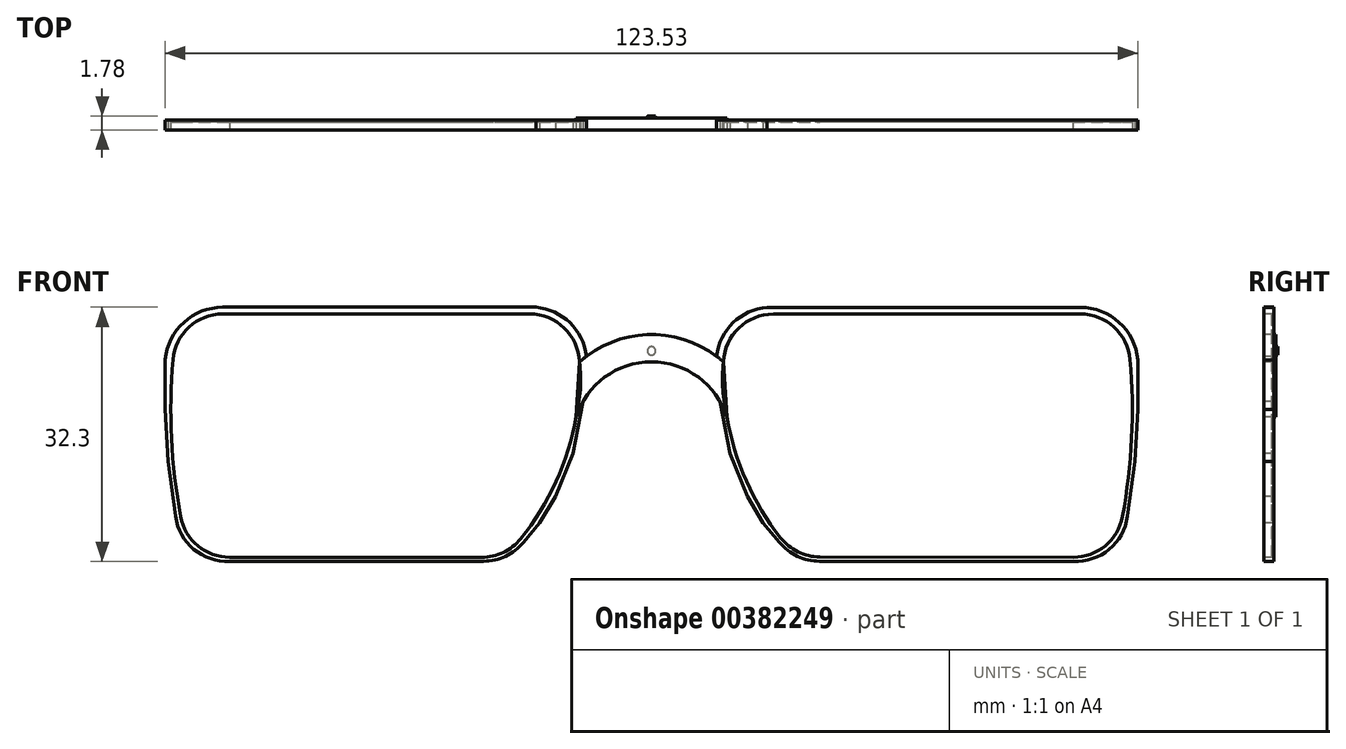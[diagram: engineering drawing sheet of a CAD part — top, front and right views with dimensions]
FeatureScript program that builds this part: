
annotation { "Feature Type Name" : "Feature", "Feature Type Description" : "" }
export const myFeature = defineFeature(function(context is Context, id is Id, definition is map)
    precondition{}
    {
        {
            var Q0;
            Q0=qCreatedBy(makeId("Front.planeOp"),FACE);
            var sketch = newSketch(context, id + "F0", { "sketchPlane" : qUnion([Q0])});
            skArc(sketch, "E0", {"start": v(-45.39, 36.1) * mm, "mid": v(-45.58, 26.1) * mm, "end": v(-44.42, 16.18) * mm});
            skLineSegment(sketch, "E1", {"start": v(-38.17, 11) * mm, "end": v(-6.15, 11) * mm});
            skLineSegment(sketch, "E2", {"start": v(-39.06, 41.9) * mm, "end": v(-0.1, 41.9) * mm});
            skPoint(sketch, "E3.visualSharp", {"position": v(-44.65, 41.9) * mm});
            skArc(sketch, "E3.filletArc", {"start": v(-39.06, 41.9) * mm, "mid": v(-43.35, 40.22) * mm, "end": v(-45.39, 36.1) * mm});
            skPoint(sketch, "E4.visualSharp", {"position": v(-43.25, 11) * mm});
            skArc(sketch, "E4.filletArc", {"start": v(-44.42, 16.18) * mm, "mid": v(-42.23, 12.46) * mm, "end": v(-38.17, 11) * mm});
            skArc(sketch, "E5", {"start": v(-1.23, 13.33) * mm, "mid": v(4.57, 23.88) * mm, "end": v(6.25, 35.8) * mm});
            skArc(sketch, "E6", {"start": v(24.99, 28.8) * mm, "mid": v(15.4, 35.8) * mm, "end": v(5.8, 28.8) * mm});
            skArc(sketch, "E7", {"start": v(24.54, 35.8) * mm, "mid": v(15.4, 39.27) * mm, "end": v(6.25, 35.8) * mm});
            skPoint(sketch, "E7.startSnap0", {"position": v(15.4, 35.8) * mm});
            skPoint(sketch, "E7.endSnap0", {"position": v(15.4, 35.8) * mm});
            skArc(sketch, "E8.MirrorCS", {"start": v(31.8, 13.45) * mm, "mid": v(26.18, 23.97) * mm, "end": v(24.54, 35.77) * mm});
            skLineSegment(sketch, "E9.MirrorCS", {"start": v(68.96, 11) * mm, "end": v(36.78, 11.03) * mm});
            skLineSegment(sketch, "E10.MirrorCS", {"start": v(69.85, 41.9) * mm, "end": v(30.88, 41.88) * mm});
            skArc(sketch, "E11.MirrorCS", {"start": v(69.85, 41.9) * mm, "mid": v(74.15, 40.23) * mm, "end": v(76.18, 36.1) * mm});
            skArc(sketch, "E12.MirrorCS", {"start": v(76.18, 36.1) * mm, "mid": v(76.38, 26.1) * mm, "end": v(75.21, 16.18) * mm});
            skArc(sketch, "E13.MirrorCS", {"start": v(75.21, 16.18) * mm, "mid": v(73.03, 12.45) * mm, "end": v(68.96, 11) * mm});
            skPoint(sketch, "E14.visualSharp", {"position": v(-3.33, 11) * mm});
            skArc(sketch, "E14.filletArc", {"start": v(-6.15, 11) * mm, "mid": v(-3.43, 11.6) * mm, "end": v(-1.23, 13.33) * mm});
            skPoint(sketch, "E15.visualSharp", {"position": v(33.9, 11.04) * mm});
            skArc(sketch, "E15.filletArc", {"start": v(31.8, 13.45) * mm, "mid": v(34, 11.67) * mm, "end": v(36.78, 11.03) * mm});
            skPoint(sketch, "E16.visualSharp", {"position": v(25.33, 41.88) * mm});
            skArc(sketch, "E16.filletArc", {"start": v(30.88, 41.88) * mm, "mid": v(26.48, 40.1) * mm, "end": v(24.54, 35.77) * mm});
            skPoint(sketch, "E17.visualSharp", {"position": v(5.43, 41.9) * mm});
            skArc(sketch, "E17.filletArc", {"start": v(6.25, 35.8) * mm, "mid": v(4.3, 40.13) * mm, "end": v(-0.1, 41.9) * mm});
            skLineSegment(sketch, "E18", {"start": v(6.25, 35.8) * mm, "end": v(5.8, 28.8) * mm});
            skLineSegment(sketch, "E19", {"start": v(24.54, 35.77) * mm, "end": v(24.99, 28.8) * mm});
            skArc(sketch, "E20", {"start": v(24.54, 35.77) * mm, "mid": v(24.46, 32.26) * mm, "end": v(24.99, 28.8) * mm});
            skArc(sketch, "E21", {"start": v(5.8, 28.8) * mm, "mid": v(6.35, 32.28) * mm, "end": v(6.25, 35.8) * mm});
            skArc(sketch, "E22", {"start": v(7.11, 36.51) * mm, "mid": v(5.03, 40.79) * mm, "end": v(0.7, 42.76) * mm});
            skLineSegment(sketch, "E23", {"start": v(0.7, 42.76) * mm, "end": v(-39.06, 42.76) * mm});
            skArc(sketch, "E24", {"start": v(-39.06, 42.76) * mm, "mid": v(-44, 40.84) * mm, "end": v(-46.37, 36.1) * mm});
            skLineSegment(sketch, "E25", {"start": v(-46.37, 36.1) * mm, "end": v(-46.37, 29.82) * mm});
            skLineSegment(sketch, "E26", {"start": v(-46.37, 29.82) * mm, "end": v(-45.98, 23.16) * mm});
            skLineSegment(sketch, "E27", {"start": v(-45.98, 23.16) * mm, "end": v(-45.07, 16.23) * mm});
            skArc(sketch, "E28", {"start": v(-45.07, 16.23) * mm, "mid": v(-42.75, 12) * mm, "end": v(-38.17, 10.5) * mm});
            skLineSegment(sketch, "E29", {"start": v(-38.17, 10.5) * mm, "end": v(-5.95, 10.5) * mm});
            skArc(sketch, "E30", {"start": v(-5.95, 10.5) * mm, "mid": v(-3.14, 11.12) * mm, "end": v(-0.87, 12.88) * mm});
            skLineSegment(sketch, "E31", {"start": v(-0.87, 12.88) * mm, "end": v(1.2, 15.37) * mm});
            skLineSegment(sketch, "E32", {"start": v(1.2, 15.37) * mm, "end": v(3.18, 18.75) * mm});
            skLineSegment(sketch, "E33", {"start": v(3.18, 18.75) * mm, "end": v(5.42, 24.2) * mm});
            skLineSegment(sketch, "E34", {"start": v(5.42, 24.2) * mm, "end": v(6.68, 30.78) * mm});
            skLineSegment(sketch, "E35.MirrorCS", {"start": v(25.36, 24.18) * mm, "end": v(24.11, 30.76) * mm});
            skLineSegment(sketch, "E36.MirrorCS", {"start": v(27.6, 18.74) * mm, "end": v(25.36, 24.18) * mm});
            skLineSegment(sketch, "E37.MirrorCS", {"start": v(29.58, 15.36) * mm, "end": v(27.6, 18.74) * mm});
            skLineSegment(sketch, "E38.MirrorCS", {"start": v(31.65, 12.87) * mm, "end": v(29.58, 15.36) * mm});
            skArc(sketch, "E39.MirrorCS", {"start": v(36.73, 10.48) * mm, "mid": v(33.93, 11.11) * mm, "end": v(31.65, 12.87) * mm});
            skLineSegment(sketch, "E40.MirrorCS", {"start": v(68.96, 10.47) * mm, "end": v(36.73, 10.48) * mm});
            skArc(sketch, "E41.MirrorCS", {"start": v(75.86, 16.21) * mm, "mid": v(73.53, 12) * mm, "end": v(68.96, 10.47) * mm});
            skLineSegment(sketch, "E42.MirrorCS", {"start": v(76.77, 23.14) * mm, "end": v(75.86, 16.21) * mm});
            skLineSegment(sketch, "E43.MirrorCS", {"start": v(77.15, 29.8) * mm, "end": v(76.77, 23.14) * mm});
            skLineSegment(sketch, "E44.MirrorCS", {"start": v(77.16, 36.08) * mm, "end": v(77.15, 29.8) * mm});
            skArc(sketch, "E45.MirrorCS", {"start": v(69.85, 42.74) * mm, "mid": v(74.8, 40.82) * mm, "end": v(77.16, 36.08) * mm});
            skLineSegment(sketch, "E46.MirrorCS", {"start": v(30.09, 42.75) * mm, "end": v(69.85, 42.74) * mm});
            skArc(sketch, "E47.MirrorCS", {"start": v(23.68, 36.5) * mm, "mid": v(25.76, 40.78) * mm, "end": v(30.09, 42.75) * mm});
            skLineSegment(sketch, "E48", {"start": v(23.68, 36.5) * mm, "end": v(23.68, 36.5) * mm});
            skLineSegment(sketch, "E49", {"start": v(24.11, 30.76) * mm, "end": v(24.12, 30.76) * mm});
            skSolve(sketch);
        }
        {
            var Q0;
            Q0=makeQuery(id+"F0.imprint","IMPRINT",FACE,{"disambiguationData":[TD([[makeQuery(id+"F0.imprint","IMPRINT",EDGE,{"derivedFrom":sQuery(id+"F0.wireOp",EDGE,"E6")}),-1.0]])]});
            extrude(context, id + "F1", {"entities" : qUnion([Q0]), "oppositeDirection" : true, "depth" : 1.52 * mm});
        }
        {
            var Q0;
            Q0=makeQuery(id+"F0.imprint","IMPRINT",FACE,{"disambiguationData":[TD([[makeQuery(id+"F0.imprint","IMPRINT",EDGE,{"derivedFrom":sQuery(id+"F0.wireOp",EDGE,"E9.MirrorCS")}),-1.0]])]});
            extrude(context, id + "F2", {"entities" : qUnion([Q0]), "oppositeDirection" : true, "depth" : 1.02 * mm});
        }
        {
            var Q0;
            Q0=makeQuery(id+"F0.imprint","IMPRINT",FACE,{"disambiguationData":[TD([[makeQuery(id+"F0.imprint","IMPRINT",EDGE,{"derivedFrom":sQuery(id+"F0.wireOp",EDGE,"E0")}),1.0]])]});
            extrude(context, id + "F3", {"entities" : qUnion([Q0]), "oppositeDirection" : true, "depth" : 1.02 * mm});
        }
        {
            var Q0;
            Q0=makeQuery(id+"F0.imprint","IMPRINT",FACE,{"disambiguationData":[TD([[makeQuery(id+"F0.imprint","IMPRINT",EDGE,{"derivedFrom":sQuery(id+"F0.wireOp",EDGE,"E0")}),-1.0]])]});
            var Q1;
            Q1=makeQuery(id+"F0.imprint","IMPRINT",FACE,{"disambiguationData":[TD([[makeQuery(id+"F0.imprint","IMPRINT",EDGE,{"derivedFrom":sQuery(id+"F0.wireOp",EDGE,"E9.MirrorCS")}),1.0]])]});
            extrude(context, id + "F4", {"entities" : qUnion([Q0, Q1]), "oppositeDirection" : true, "depth" : 1.27 * mm});
        }
        {
            var Q0;
            Q0=makeQuery(id+"F1.opExtrude","CAP_FACE",FACE,{"disambiguationData":[OSD([sQuery(id+"F0.wireOp",EDGE,"E6"),sQuery(id+"F0.wireOp",EDGE,"E7"),sQuery(id+"F0.wireOp",EDGE,"E16.filletArc"),sQuery(id+"F0.wireOp",EDGE,"E20"),sQuery(id+"F0.wireOp",EDGE,"E21"),sQuery(id+"F0.wireOp",EDGE,"E47.MirrorCS"),sQuery(id+"F0.wireOp",EDGE,"E48")])],"isStart":false});
            var sketch = newSketch(context, id + "F5", { "sketchPlane" : qUnion([Q0])});
            skCircle(sketch, "E50", {"center": v(-15.4, 37.2) * mm, "radius": 0.53 * mm});
            skPoint(sketch, "E50.centerSnap0", {"position": v(-15.4, 35.8) * mm});
            skSolve(sketch);
        }
        {
            var Q0;
            Q0=makeQuery(id+"F5.imprint","IMPRINT",FACE,{"disambiguationData":[TD([[makeQuery(id+"F5.imprint","IMPRINT",EDGE,{"derivedFrom":sQuery(id+"F5.wireOp",EDGE,"E50")}),1.0]])]});
            extrude(context, id + "F6", {"entities" : qUnion([Q0]), "operationType" : NewBodyOperationType.ADD, "depth" : 0.25 * mm});
        }
    });
